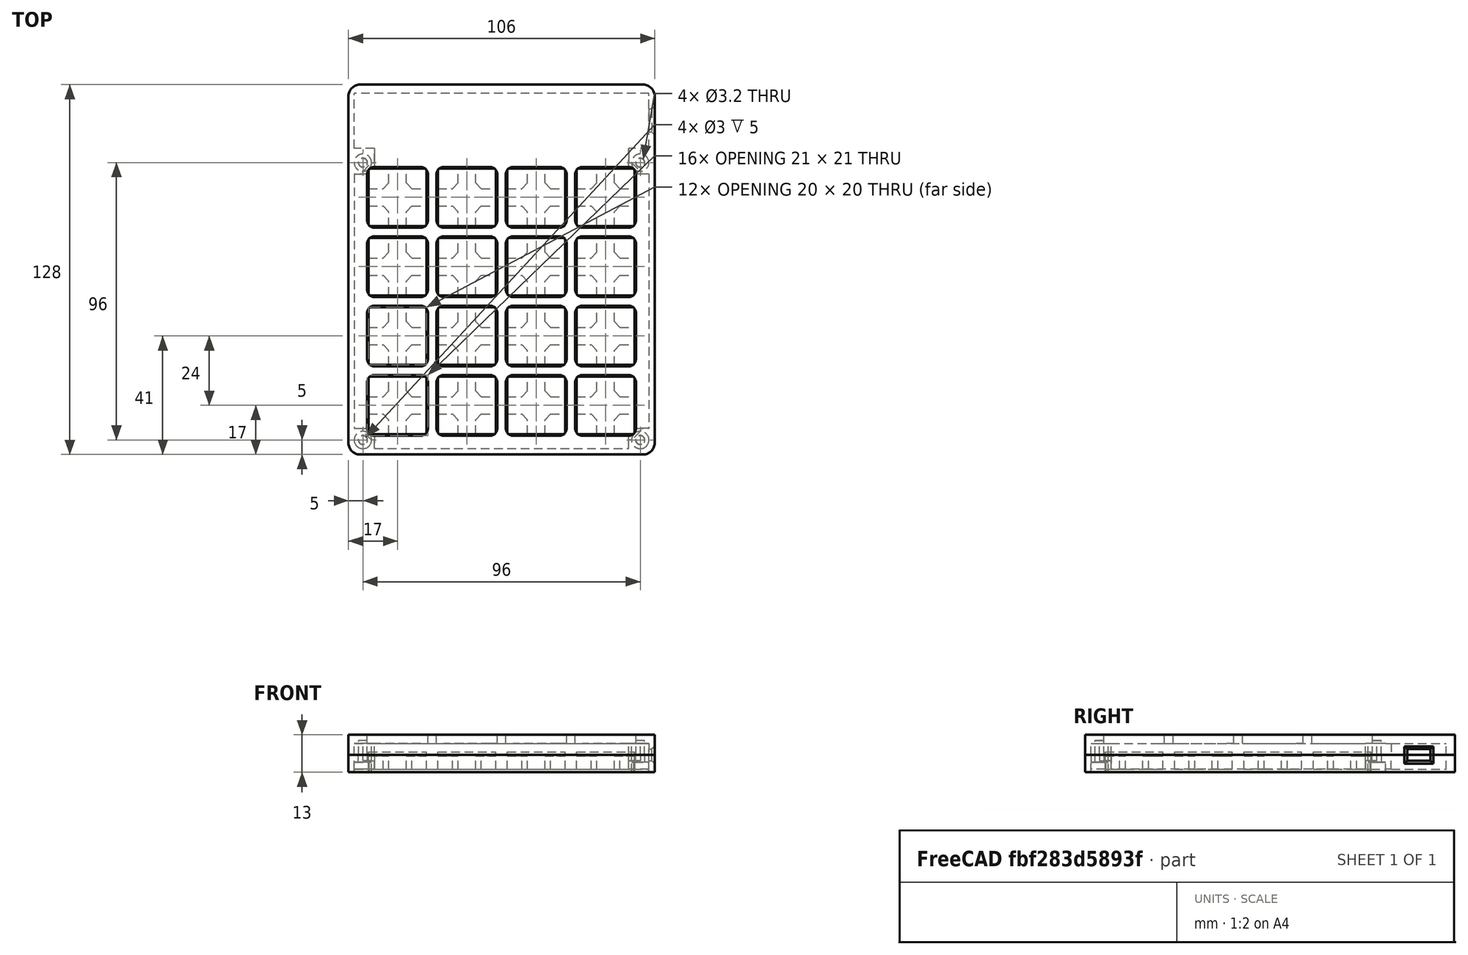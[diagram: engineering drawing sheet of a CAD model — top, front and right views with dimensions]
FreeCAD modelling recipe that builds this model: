
FCSTD DOCUMENT  (FreeCAD 0.16R6700 (Git))
Label: parametric_pad_base
License: All rights reserved
LicenseURL: http://en.wikipedia.org/wiki/All_rights_reserved
objects: Part::Box×25, Part::Cut×16, Part::FeaturePython×11, Part::MultiFuse×10, Part::Chamfer×7, Part::Fillet×4, Part::Cylinder×3, Spreadsheet::Sheet×1, Part::Offset×1
note: 77 computed .brp shape members not serialized (recipe doc carries the construction recipe); baked Part::Feature solids carry a one-line shape summary decoded from their .brp

FEATURE [Spreadsheet::Sheet] Spreadsheet  label="data"
  cells = A2=Button safe height; B2(button_safe_height)=4.6; C2=Pad size; D2(pad_size)=20; A3=N rows pad; B3(rows_pad)=4; A4=N columns pad; B4(columns_pad)=4; A5=Space between pads; B5(space_between_pads)=4; A6=Border; B6(border)=7; A7=Shell; B7(shell)=2; A9=Electronics length; B9(electronics_length)=103; A10=Electronics width; B10(electronics_width)=22
FEATURE [Part::Box] Box004  label="base_bot"
  Height = 1
  Length = 106
  Placement = pos=(-7,-7,0) rot=(0,0,1;0rad)
  Width = 106
  expr: Placement.Base.x = -data.border
  expr: Placement.Base.y = -data.border
  expr: Length = data.columns_pad * data.pad_size + data.space_between_pads * (data.columns_pad - 1) + 2 * data.border
  expr: Width = data.rows_pad * data.pad_size + data.space_between_pads * (data.rows_pad - 1) + 2 * data.border
FEATURE [Part::Box] Box005  label="Cube004"
  Height = 6
  Length = 106
  Placement = pos=(-7,-7,0) rot=(0,0,1;0rad)
  Width = 106
  expr: Placement.Base.y = -data.border
  expr: Placement.Base.x = -data.border
  expr: Width = data.rows_pad * data.pad_size + data.space_between_pads * (data.rows_pad - 1) + 2 * data.border
  expr: Length = data.columns_pad * data.pad_size + data.space_between_pads * (data.columns_pad - 1) + 2 * data.border
FEATURE [Part::Box] Box006  label="Cube005"
  Height = 10
  Length = 102
  Placement = pos=(-5,-5,0) rot=(0,0,1;0rad)
  Width = 102
  expr: Placement.Base.x = -data.border + data.shell
  expr: Placement.Base.y = -data.border + data.shell
  expr: Width = data.rows_pad * data.pad_size + data.space_between_pads * (data.rows_pad - 1) + 2 * data.border - 2 * data.shell
  expr: Length = data.columns_pad * data.pad_size + data.space_between_pads * (data.columns_pad - 1) + 2 * data.border - 2 * data.shell
FEATURE [Part::Cut] Cut001  label="outdoor_wall"
  Base = -> Box005
  Tool = -> Box006
FEATURE [Part::Box] Box003  label="Cube003"
  Height = 1
  Length = 20
  Width = 20
  expr: Width = data.pad_size
  expr: Length = data.pad_size
FEATURE [Part::Box] Box002  label="Cube002"
  Height = 10
  Length = 20
  Placement = pos=(0,7,0) rot=(0,0,1;0rad)
  Width = 6
  expr: Placement.Base.y = data.pad_size - 13
  expr: Length = data.pad_size
FEATURE [Part::Box] Box001  label="Cube001"
  Height = 10
  Length = 6
  Placement = pos=(7,0,0) rot=(0,0,1;0rad)
  Width = 20
  expr: Placement.Base.x = data.pad_size - 13
  expr: Width = data.pad_size
FEATURE [Part::MultiFuse] Fusion
  Shapes = -> [Box001,Box002]
FEATURE [Part::Box] Box  label="Cube"
  Height = 4.6
  Length = 20
  Width = 20
  expr: Width = data.pad_size
  expr: Length = data.pad_size
  expr: Height = data.button_safe_height
FEATURE [Part::Cut] Cut
  Base = -> Box
  Tool = -> Fusion
FEATURE [Part::Chamfer] Chamfer  label="base_button"
  Base = -> Cut
  Edges = 4 edges r=2: [Edge9,Edge24,Edge35,Edge41]
  Placement = pos=(0,0,1) rot=(0,0,1;0rad)
FEATURE [Part::MultiFuse] Fusion001  label="single_pad_base"
  Shapes = -> [Box003,Chamfer]
FEATURE [Part::FeaturePython] Array  label="button_bases"  # Draft array (typed FeaturePython)
  Angle = 360
  ArrayType = 0
  Axis = (0,0,1)
  Base = -> Fusion001
  Center = (0,0,0)
  Fuse = false
  IntervalAxis = (0,0,0)
  IntervalX = (24,0,0)
  IntervalY = (0,24,0)
  IntervalZ = (0,0,0)
  NumberPolar = 1
  NumberX = 4
  NumberY = 4
  NumberZ = 1
  expr: IntervalX.x = data.space_between_pads + data.pad_size
  expr: NumberY = data.rows_pad
  expr: IntervalY.y = data.space_between_pads + data.pad_size
  expr: NumberX = data.columns_pad
FEATURE [Part::Box] Box007  label="Cube006"
  Height = 1
  Length = 20
  Placement = pos=(0,0,6) rot=(0,0,1;0rad)
  Width = 20
  expr: Width = data.pad_size
  expr: Length = data.pad_size
FEATURE [Part::FeaturePython] Array001  label="led_bases"  # Draft array (typed FeaturePython)
  Angle = 360
  ArrayType = 0
  Axis = (0,0,1)
  Base = -> Box007
  Center = (0,0,0)
  Fuse = false
  IntervalAxis = (0,0,0)
  IntervalX = (24,0,0)
  IntervalY = (0,24,0)
  IntervalZ = (0,0,0)
  NumberPolar = 1
  NumberX = 4
  NumberY = 4
  NumberZ = 1
  expr: IntervalX.x = data.space_between_pads + data.pad_size
  expr: NumberY = data.rows_pad
  expr: IntervalY.y = data.space_between_pads + data.pad_size
  expr: NumberX = data.columns_pad
FEATURE [Part::Box] Box008  label="Cube007"
  Height = 8
  Length = 20
  Placement = pos=(0,0,7) rot=(0,0,1;0rad)
  Width = 20
  expr: Width = data.pad_size
  expr: Length = data.pad_size
FEATURE [Part::Fillet] Fillet  label="corners_Fillet"
  Base = -> Box008
  Edges = 4 edges r=2: [Edge1,Edge3,Edge5,Edge7]
FEATURE [Part::Fillet] Fillet001  label="top_Fillet"
  Base = -> Fillet
  Edges = 8 edges r=1: [Edge1,Edge5,Edge6,Edge7,Edge8,Edge9,Edge10,Edge11]
FEATURE [Part::Cylinder] Cylinder
  Angle = 360
  Height = 6
  Placement = pos=(-3,-3,0) rot=(0,0,1;0rad)
  Radius = 1.6
  expr: Placement.Base.y = -data.border + 4
  expr: Placement.Base.x = -data.border + 4
FEATURE [Part::Box] Box009  label="Cube008"
  Height = 6
  Length = 9
  Placement = pos=(-7,-7,0) rot=(0,0,1;0rad)
  Width = 9
  expr: Placement.Base.y = -data.border
  expr: Placement.Base.x = -data.border
FEATURE [Part::Cylinder] Cylinder001
  Angle = 360
  Height = 3.5
  Placement = pos=(-3,-3,0) rot=(0,0,1;0rad)
  Radius = 3
  expr: Placement.Base.y = -data.border + 4
  expr: Placement.Base.x = -data.border + 4
FEATURE [Part::MultiFuse] Fusion002  label="screw"
  Placement = pos=(1,1,0) rot=(0,0,1;0rad)
  Shapes = -> [Cylinder,Cylinder001]
FEATURE [Part::Box] Box010  label="Cube009"
  Height = 10
  Length = 10
  Placement = pos=(-2,-2,4) rot=(0,0,1;0rad)
  Width = 10
  expr: Placement.Base.y = -data.border + 5
  expr: Placement.Base.x = -data.border + 5
FEATURE [Part::Chamfer] Chamfer001
  Base = -> Box010
  Edges = 1 edges r=3: [Edge1]
FEATURE [Part::Cut] Cut002
  Base = -> Box009
  Tool = -> Chamfer001
FEATURE [Part::FeaturePython] Array004  # Draft array (typed FeaturePython)
  Angle = 360
  ArrayType = 1
  Axis = (0,0,1)
  Base = -> Cut002
  Center = (-7,-7,0)
  Fuse = false
  IntervalAxis = (106,106,0)
  IntervalX = (1,0,0)
  IntervalY = (0,1,0)
  IntervalZ = (0,0,0)
  NumberPolar = 2
  NumberX = 2
  NumberY = 2
  NumberZ = 1
  expr: Center.y = -data.border
  expr: Center.x = -data.border
  expr: IntervalAxis.x = data.columns_pad * data.pad_size + data.space_between_pads * (data.columns_pad - 1) + 2 * data.border
  expr: IntervalAxis.y = data.rows_pad * data.pad_size + data.space_between_pads * (data.rows_pad - 1) + 2 * data.border
FEATURE [Part::Cut] Cut003
  Base = -> Box009
  Tool = -> Chamfer001
FEATURE [Part::FeaturePython] Array005  # Draft array (typed FeaturePython)
  Angle = 90
  ArrayType = 1
  Axis = (0,0,1)
  Base = -> Cut003
  Center = (-7,-7,0)
  Fuse = false
  IntervalAxis = (106,0,0)
  IntervalX = (1,0,0)
  IntervalY = (0,1,0)
  IntervalZ = (0,0,0)
  NumberPolar = 2
  NumberX = 2
  NumberY = 2
  NumberZ = 1
  expr: Center.y = -data.border
  expr: Center.x = -data.border
  expr: IntervalAxis.x = data.columns_pad * data.pad_size + data.space_between_pads * (data.columns_pad - 1) + 2 * data.border
FEATURE [Part::Cut] Cut004
  Base = -> Box009
  Tool = -> Chamfer001
FEATURE [Part::FeaturePython] Array006  # Draft array (typed FeaturePython)
  Angle = -90
  ArrayType = 1
  Axis = (0,0,1)
  Base = -> Cut004
  Center = (-7,-7,0)
  Fuse = false
  IntervalAxis = (0,106,0)
  IntervalX = (1,0,0)
  IntervalY = (0,1,0)
  IntervalZ = (0,0,0)
  NumberPolar = 2
  NumberX = 2
  NumberY = 2
  NumberZ = 1
  expr: Center.x = -data.border
  expr: Center.y = -data.border
  expr: IntervalAxis.y = data.rows_pad * data.pad_size + data.space_between_pads * (data.rows_pad - 1) + 2 * data.border
FEATURE [Part::FeaturePython] Array007  label="screws"  # Draft array (typed FeaturePython)
  Angle = 360
  ArrayType = 0
  Axis = (0,0,1)
  Base = -> Fusion002
  Center = (0,0,0)
  Fuse = false
  IntervalAxis = (0,0,0)
  IntervalX = (96,0,0)
  IntervalY = (0,96,0)
  IntervalZ = (0,0,0)
  NumberPolar = 2
  NumberX = 2
  NumberY = 2
  NumberZ = 1
  expr: IntervalY.y = data.rows_pad * data.pad_size + data.space_between_pads * (data.rows_pad - 1) + 2 * data.border - 10
  expr: IntervalX.x = data.columns_pad * data.pad_size + data.space_between_pads * (data.columns_pad - 1) + 2 * data.border - 10
FEATURE [Part::Box] Box011  label="electronics_enclosure_bot"
  Height = 6
  Length = 106
  Placement = pos=(-7,97,0) rot=(0,0,1;0rad)
  Width = 24
  expr: Width = data.electronics_width + data.shell
  expr: Length = data.columns_pad * data.pad_size + data.space_between_pads * (data.columns_pad - 1) + 2 * data.border
  expr: Placement.Base.y = -2 - data.border + data.rows_pad * data.pad_size + data.space_between_pads * (data.rows_pad - 1) + 2 * data.border
  expr: Placement.Base.x = -data.border
FEATURE [Part::Box] Box012  label="electronics_space_bot"
  Height = 6
  Length = 102
  Placement = pos=(-5,97,1) rot=(0,0,1;0rad)
  Width = 21
  expr: Width = data.electronics_width - data.shell / 2
  expr: Length = data.columns_pad * data.pad_size + data.space_between_pads * (data.columns_pad - 1) + 2 * data.border - 2 * data.shell
  expr: Placement.Base.x = -data.border + data.shell
  expr: Placement.Base.y = -2 - data.border + data.rows_pad * data.pad_size + data.space_between_pads * (data.rows_pad - 1) + 2 * data.border
FEATURE [Part::MultiFuse] Fusion004  label="base_+_electronics_enclosure"
  Shapes = -> [Cut001,Box004,Box011]
FEATURE [Part::Cut] Cut005  label="base_electronics_Ready"
  Base = -> Fusion004
  Tool = -> Box012
FEATURE [Part::MultiFuse] Fusion005  label="corners_bot"
  Shapes = -> [Array006,Array004,Array005]
FEATURE [Part::MultiFuse] Fusion006  label="base_no_screw_holes"
  Shapes = -> [Fusion005,Cut005]
FEATURE [Part::Cut] Cut006  label="base_screw_holes"
  Base = -> Fusion006
  Tool = -> Array007
FEATURE [Part::Box] Box013  label="Cube010"
  Height = 7
  Length = 106
  Placement = pos=(-7,-7,6) rot=(0,0,1;0rad)
  Width = 106
  expr: Width = data.rows_pad * data.pad_size + data.space_between_pads * (data.rows_pad - 1) + 2 * data.border
  expr: Length = data.columns_pad * data.pad_size + data.space_between_pads * (data.columns_pad - 1) + 2 * data.border
  expr: Placement.Base.y = -data.border
  expr: Placement.Base.x = -data.border
FEATURE [Part::Box] Box014  label="Cube011"
  Height = 4
  Length = 102
  Placement = pos=(-5,-5,6) rot=(0,0,1;0rad)
  Width = 102
  expr: Placement.Base.y = -data.border + data.shell
  expr: Height = 7 - data.shell - 1
  expr: Placement.Base.x = -data.border + data.shell
  expr: Length = data.columns_pad * data.pad_size + data.space_between_pads * (data.columns_pad - 1) + 2 * data.border - 2 * data.shell
  expr: Width = data.rows_pad * data.pad_size + data.space_between_pads * (data.rows_pad - 1) + 2 * data.border - 2 * data.shell
FEATURE [Part::Cut] Cut007  label="base_top"
  Base = -> Box013
  Tool = -> Box014
FEATURE [Part::Offset] Offset
  Fill = false
  Intersection = false
  Join = 0
  Mode = 0
  SelfIntersection = false
  Source = -> Fillet001
  Value = 0.5
FEATURE [Part::FeaturePython] Array008  label="silicone_pads"  # Draft array (typed FeaturePython)
  Angle = 360
  ArrayType = 0
  Axis = (0,0,1)
  Base = -> Offset
  Center = (0,0,0)
  Fuse = false
  IntervalAxis = (0,0,0)
  IntervalX = (24,0,0)
  IntervalY = (0,24,0)
  IntervalZ = (0,0,0)
  NumberPolar = 1
  NumberX = 4
  NumberY = 4
  NumberZ = 1
  expr: NumberY = data.rows_pad
  expr: NumberX = data.columns_pad
  expr: IntervalY.y = data.space_between_pads + data.pad_size
  expr: IntervalX.x = data.space_between_pads + data.pad_size
FEATURE [Part::Cut] Cut008  label="base_top_pad_holed"
  Base = -> Cut007
  Tool = -> Array008
FEATURE [Part::Fillet] Fillet002  label="base_corners_fillet"
  Base = -> Cut006
  Edges = 6 edges r=4: [Edge82,Edge141,Edge171,Edge198,Edge200,Edge207]
FEATURE [Part::MultiFuse] Fusion007  label="bot_part_no_usb_hole"
  Shapes = -> [Array,Fillet002]
FEATURE [Part::Box] Box015  label="electronics_enclosure_top"
  Height = 7
  Length = 106
  Placement = pos=(-7,97,6) rot=(0,0,1;0rad)
  Width = 24
  expr: Width = data.electronics_width + data.shell
  expr: Length = data.columns_pad * data.pad_size + data.space_between_pads * (data.columns_pad - 1) + 2 * data.border
  expr: Placement.Base.y = -2 - data.border + data.rows_pad * data.pad_size + data.space_between_pads * (data.rows_pad - 1) + 2 * data.border
  expr: Placement.Base.x = -data.border
FEATURE [Part::Box] Box016  label="electronics_space_top"
  Height = 5
  Length = 102
  Placement = pos=(-5,97,5) rot=(0,0,1;0rad)
  Width = 21
  expr: Width = data.electronics_width - data.shell / 2
  expr: Length = data.columns_pad * data.pad_size + data.space_between_pads * (data.columns_pad - 1) + 2 * data.border - 2 * data.shell
  expr: Placement.Base.y = -2 - data.border + data.rows_pad * data.pad_size + data.space_between_pads * (data.rows_pad - 1) + 2 * data.border
  expr: Placement.Base.x = -data.border + data.shell
FEATURE [Part::MultiFuse] Fusion008  label="base_top_+_electronics_enclosure"
  Shapes = -> [Cut008,Box015]
FEATURE [Part::Cut] Cut009  label="base_top_electronics_ready"
  Base = -> Fusion008
  Tool = -> Box016
FEATURE [Part::Box] Box017  label="Cube012"
  Height = 7
  Length = 9
  Placement = pos=(-7,-7,6) rot=(0,0,1;0rad)
  Width = 9
  expr: Placement.Base.y = -data.border
  expr: Placement.Base.x = -data.border
FEATURE [Part::Box] Box018  label="Cube013"
  Height = 10
  Length = 10
  Placement = pos=(-2,-2,4) rot=(0,0,1;0rad)
  Width = 10
  expr: Placement.Base.y = -data.border + 5
  expr: Placement.Base.x = -data.border + 5
FEATURE [Part::Chamfer] Chamfer002
  Base = -> Box018
  Edges = 1 edges r=3: [Edge1]
FEATURE [Part::Cut] Cut010
  Base = -> Box017
  Tool = -> Chamfer002
FEATURE [Part::Box] Box019  label="Cube014"
  Height = 10
  Length = 10
  Placement = pos=(-2,-2,4) rot=(0,0,1;0rad)
  Width = 10
  expr: Placement.Base.y = -data.border + 5
  expr: Placement.Base.x = -data.border + 5
FEATURE [Part::Box] Box020  label="Cube015"
  Height = 7
  Length = 9
  Placement = pos=(-7,-7,6) rot=(0,0,1;0rad)
  Width = 9
  expr: Placement.Base.y = -data.border
  expr: Placement.Base.x = -data.border
FEATURE [Part::Chamfer] Chamfer003
  Base = -> Box019
  Edges = 1 edges r=3: [Edge1]
FEATURE [Part::Cut] Cut011
  Base = -> Box020
  Tool = -> Chamfer003
FEATURE [Part::Box] Box021  label="Cube016"
  Height = 10
  Length = 10
  Placement = pos=(-2,-2,4) rot=(0,0,1;0rad)
  Width = 10
  expr: Placement.Base.y = -data.border + 5
  expr: Placement.Base.x = -data.border + 5
FEATURE [Part::Box] Box022  label="Cube017"
  Height = 7
  Length = 9
  Placement = pos=(-7,-7,6) rot=(0,0,1;0rad)
  Width = 9
  expr: Placement.Base.y = -data.border
  expr: Placement.Base.x = -data.border
FEATURE [Part::Chamfer] Chamfer004
  Base = -> Box021
  Edges = 1 edges r=3: [Edge1]
FEATURE [Part::Cut] Cut012
  Base = -> Box022
  Tool = -> Chamfer004
FEATURE [Part::FeaturePython] Array009  # Draft array (typed FeaturePython)
  Angle = -90
  ArrayType = 1
  Axis = (0,0,1)
  Base = -> Cut010
  Center = (-7,-7,0)
  Fuse = false
  IntervalAxis = (0,106,0)
  IntervalX = (1,0,0)
  IntervalY = (0,1,0)
  IntervalZ = (0,0,0)
  NumberPolar = 2
  NumberX = 2
  NumberY = 2
  NumberZ = 1
  expr: Center.y = -data.border
  expr: Center.x = -data.border
  expr: IntervalAxis.y = data.rows_pad * data.pad_size + data.space_between_pads * (data.rows_pad - 1) + 2 * data.border
FEATURE [Part::FeaturePython] Array010  # Draft array (typed FeaturePython)
  Angle = 360
  ArrayType = 1
  Axis = (0,0,1)
  Base = -> Cut011
  Center = (-7,-7,0)
  Fuse = false
  IntervalAxis = (106,106,0)
  IntervalX = (1,0,0)
  IntervalY = (0,1,0)
  IntervalZ = (0,0,0)
  NumberPolar = 2
  NumberX = 2
  NumberY = 2
  NumberZ = 1
  expr: IntervalAxis.y = data.rows_pad * data.pad_size + data.space_between_pads * (data.rows_pad - 1) + 2 * data.border
  expr: IntervalAxis.x = data.columns_pad * data.pad_size + data.space_between_pads * (data.columns_pad - 1) + 2 * data.border
  expr: Center.y = -data.border
  expr: Center.x = -data.border
FEATURE [Part::FeaturePython] Array011  # Draft array (typed FeaturePython)
  Angle = 90
  ArrayType = 1
  Axis = (0,0,1)
  Base = -> Cut012
  Center = (-7,-7,0)
  Fuse = false
  IntervalAxis = (106,0,0)
  IntervalX = (1,0,0)
  IntervalY = (0,1,0)
  IntervalZ = (0,0,0)
  NumberPolar = 2
  NumberX = 2
  NumberY = 2
  NumberZ = 1
  expr: IntervalAxis.x = data.columns_pad * data.pad_size + data.space_between_pads * (data.columns_pad - 1) + 2 * data.border
  expr: Center.y = -data.border
  expr: Center.x = -data.border
FEATURE [Part::MultiFuse] Fusion009  label="corners_top"
  Shapes = -> [Array009,Array010,Array011]
FEATURE [Part::Cylinder] Cylinder002
  Angle = 360
  Height = 5
  Placement = pos=(-2,-2,6) rot=(0,0,1;0rad)
  Radius = 1.5
  expr: Placement.Base.y = -data.border + 5
  expr: Placement.Base.x = -data.border + 5
FEATURE [Part::FeaturePython] Array012  label="screws_top"  # Draft array (typed FeaturePython)
  Angle = 360
  ArrayType = 0
  Axis = (0,0,1)
  Base = -> Cylinder002
  Center = (0,0,0)
  Fuse = false
  IntervalAxis = (0,0,0)
  IntervalX = (96,0,0)
  IntervalY = (0,96,0)
  IntervalZ = (0,0,0)
  NumberPolar = 1
  NumberX = 2
  NumberY = 2
  NumberZ = 1
  expr: IntervalY.y = data.rows_pad * data.pad_size + data.space_between_pads * (data.rows_pad - 1) + 2 * data.border - 10
  expr: IntervalX.x = data.columns_pad * data.pad_size + data.space_between_pads * (data.columns_pad - 1) + 2 * data.border - 10
FEATURE [Part::MultiFuse] Fusion010  label="base_top_no_screw_holes"
  Shapes = -> [Cut009,Fusion009]
FEATURE [Part::Cut] Cut013  label="base_top_screw_holes"
  Base = -> Fusion010
  Tool = -> Array012
FEATURE [Part::Fillet] Fillet003  label="base_top_corners_fillet"
  Base = -> Cut013
  Edges = 4 edges r=4: [Edge2,Edge4,Edge564,Edge565]
FEATURE [Part::Box] Box023  label="Cube018"
  Height = 4
  Length = 8
  Placement = pos=(96,104.5,4) rot=(0,0,1;0rad)
  Width = 8
  expr: Placement.Base.x = data.columns_pad * (data.pad_size + data.space_between_pads)
  expr: Placement.Base.y = -2 - data.border + data.rows_pad * data.pad_size + data.space_between_pads * (data.rows_pad - 1) + 2 * data.border + data.electronics_width / 2 - 3.5
FEATURE [Part::Cut] Cut014  label="base_top_no_chanfer"
  Base = -> Fillet003
  Tool = -> Box023
FEATURE [Part::Chamfer] Chamfer005  label="top_part"
  Base = -> Cut014
  Edges = 3 edges r=1: [Edge23,Edge24,Edge25]
FEATURE [Part::Box] Box024  label="Cube019"
  Height = 4
  Length = 8
  Placement = pos=(96,104.5,4) rot=(0,0,1;0rad)
  Width = 8
  expr: Placement.Base.y = -2 - data.border + data.rows_pad * data.pad_size + data.space_between_pads * (data.rows_pad - 1) + 2 * data.border + data.electronics_width / 2 - 3.5
  expr: Placement.Base.x = data.columns_pad * (data.pad_size + data.space_between_pads)
FEATURE [Part::Cut] Cut015  label="base_bot_no_chanfer"
  Base = -> Fusion007
  Tool = -> Box024
FEATURE [Part::Chamfer] Chamfer006  label="bot_part"
  Base = -> Cut015
  Edges = 3 edges r=1: [Edge1198,Edge1200,Edge1201]
